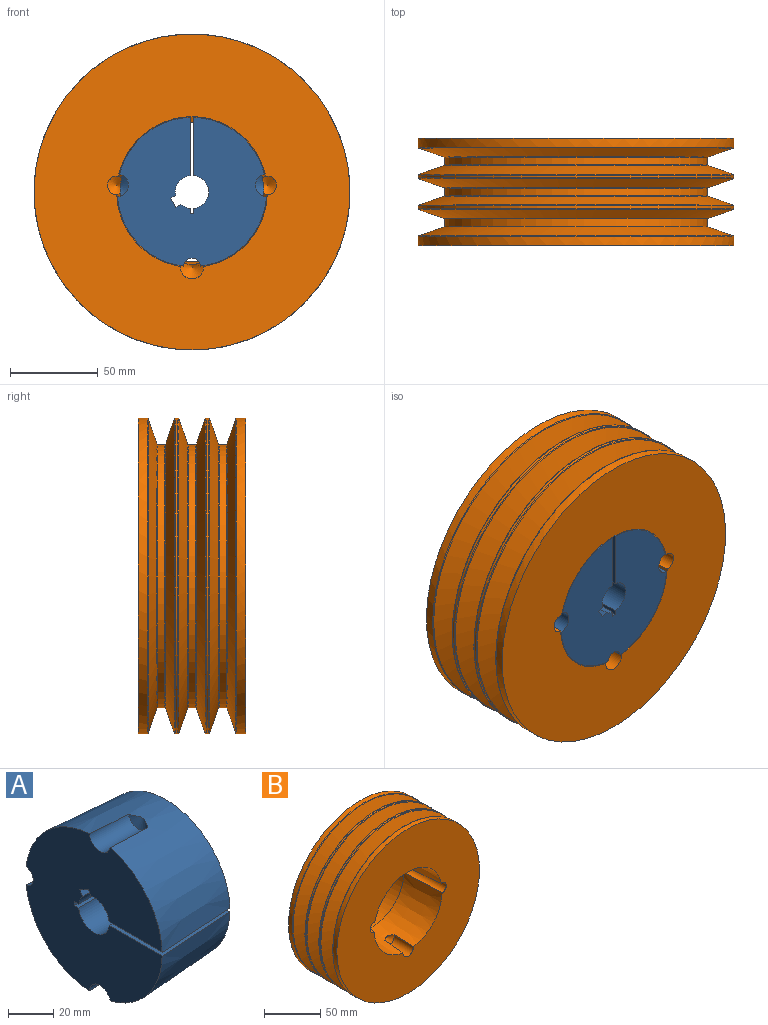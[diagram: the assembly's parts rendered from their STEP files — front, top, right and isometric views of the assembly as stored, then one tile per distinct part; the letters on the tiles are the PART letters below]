
ASSEMBLY  parts=2 mates=1
PART A: 20 faces, bbox 45x84.8x85 mm
  f0: cone r=39.69mm half-angle=3.6deg, axis (-1,0,0), area 5249.3mm2, adj f4,f6,f7,f15,f18,f19
  f1: cone r=39.69mm half-angle=3.6deg, axis (-1,0,0), area 5249.3mm2, adj f4,f6,f8,f15,f16,f17
  f2: cylinder r=9.5mm len=45mm, axis (1,0,0), area 712.9mm2, adj f4,f6,f8,f13
  f3: cylinder r=9.5mm len=45mm, axis (1,0,0), area 265.2mm2, adj f4,f6,f9,f14
  f4: plane 84.82x84.7mm, normal (-1,0,0), area 5146.6mm2, adj f0,f1,f2,f3,f5,f7,f8,f9
  f5: cylinder r=9.5mm len=45mm, axis (1,0,0), area 1252.9mm2, adj f4,f6,f7,f10
  f6: plane 79.38x79.19mm, normal (1,0,0), area 4571.4mm2, adj f0,f1,f2,f3,f5,f7,f8,f9
  f7: plane 45x33.04mm, normal (0,0,1), area 1423.5mm2, adj f0,f4,f5,f6
  f8: plane 45x33.04mm, normal (0,0,-1), area 1423.5mm2, adj f1,f2,f4,f6
  f9: plane 45x2.85mm, normal (0,0,-1), area 128.4mm2, adj f3,f4,f6,f11
  f10: plane 45x2.85mm, normal (0,0,1), area 128.4mm2, adj f4,f5,f6,f11
  f11: plane 45x2mm, normal (0,-1,0), area 90mm2, adj f4,f6,f9,f10
  f12: plane 45x5.2mm, normal (0,-0.5,-0.87), area 270mm2, adj f4,f6,f13,f14
  f13: plane 45x2.85mm, normal (0,0.87,-0.5), area 147.9mm2, adj f2,f4,f6,f12
  f14: plane 45x2.85mm, normal (0,-0.87,0.5), area 147.9mm2, adj f3,f4,f6,f12
  f15: cylinder r=5mm len=45mm, axis (1,0,0), area 515.4mm2, adj f0,f1,f4,f6
  f16: cone r=0mm half-angle=60deg, axis (-1,0,0), area 46mm2, adj f1,f17
  f17: cylinder r=6.5mm len=24mm, axis (-1,0,0), area 414.5mm2, adj f1,f4,f16
  f18: cone r=0mm half-angle=60deg, axis (-1,0,0), area 46mm2, adj f0,f19
  f19: cylinder r=6.5mm len=24mm, axis (-1,0,0), area 414.5mm2, adj f0,f4,f18
PART B: 40 faces, bbox 194.8x61x194.8 mm
  f0: plane 180x180mm, normal (0,-1,0), area 19496.2mm2, adj f1,f34,f35,f36,f38,f39
  f1: cylinder r=5.36mm len=45mm, axis (0,-1,0), area 936.2mm2, adj f0,f2,f34,f36
  f2: cone r=0mm half-angle=59deg, axis (0,-1,0), area 90.3mm2, adj f1,f3,f4,f33
  f3: cone r=42.92mm half-angle=4deg, axis (0,-1,0), area 0mm2, adj f2,f4
  f4: cylinder r=39.78mm len=79.56mm, axis (0,-1,0), area 3985.1mm2, adj f2,f3,f5,f6,f7,f8,f33,f34
  f5: cone r=42.92mm half-angle=4deg, axis (0,-1,0), area 0mm2, adj f4,f6
  f6: cone r=0mm half-angle=59deg, axis (0,-1,0), area 90.3mm2, adj f4,f5,f7,f35
  f7: cone r=42.92mm half-angle=4deg, axis (0,-1,0), area 0mm2, adj f4,f6
  f8: plane 180x180mm, normal (0,1,0), area 20475.5mm2, adj f4,f9
  f9: cylinder r=90mm len=180mm, axis (0,-1,0), area 2840.6mm2, adj f8,f10
  f10: torus R=89.5mm, axis (0,1,0), area 349.9mm2, adj f9,f11
  f11: cone r=75mm half-angle=71deg, axis (0,1,0), area 7853.7mm2, adj f10,f12
  f12: torus R=75.5mm, axis (0,-1,0), area 292.4mm2, adj f11,f13
  f13: cylinder r=75mm len=150mm, axis (0,-1,0), area 1977.7mm2, adj f12,f14
  f14: torus R=75.5mm, axis (0,-1,0), area 292.4mm2, adj f13,f15
  f15: cone r=90mm half-angle=71deg, axis (0,-1,0), area 7853.7mm2, adj f14,f16
  f16: torus R=89.5mm, axis (0,1,0), area 349.9mm2, adj f15,f17
  f17: cylinder r=90mm len=180mm, axis (0,-1,0), area 874.6mm2, adj f16,f18
  f18: torus R=89.5mm, axis (0,1,0), area 349.9mm2, adj f17,f19
  f19: cone r=75mm half-angle=71deg, axis (0,1,0), area 7853.7mm2, adj f18,f20
  f20: torus R=75.5mm, axis (0,-1,0), area 292.4mm2, adj f19,f21
  f21: cylinder r=75mm len=150mm, axis (0,-1,0), area 1977.7mm2, adj f20,f22
  f22: torus R=75.5mm, axis (0,-1,0), area 292.4mm2, adj f21,f23
  f23: cone r=90mm half-angle=71deg, axis (0,-1,0), area 7853.7mm2, adj f22,f24
  f24: torus R=89.5mm, axis (0,1,0), area 349.9mm2, adj f23,f25
  f25: cylinder r=90mm len=180mm, axis (0,-1,0), area 874.6mm2, adj f24,f26
  f26: torus R=89.5mm, axis (0,1,0), area 349.9mm2, adj f25,f27
  f27: cone r=75mm half-angle=71deg, axis (0,1,0), area 7853.7mm2, adj f26,f28
  f28: torus R=75.5mm, axis (0,-1,0), area 292.4mm2, adj f27,f29
  f29: cylinder r=75mm len=150mm, axis (0,-1,0), area 1977.7mm2, adj f28,f30
  f30: torus R=75.5mm, axis (0,-1,0), area 292.4mm2, adj f29,f31
  f31: cone r=90mm half-angle=71deg, axis (0,-1,0), area 7853.7mm2, adj f30,f32
  f32: torus R=89.5mm, axis (0,1,0), area 349.9mm2, adj f31,f39
  f33: cone r=42.92mm half-angle=4deg, axis (0,-1,0), area 0mm2, adj f2,f4
  f34: cone r=42.92mm half-angle=4deg, axis (0,-1,0), area 5088.6mm2, adj f0,f1,f4,f35
  f35: cylinder r=5.36mm len=45mm, axis (0,-1,0), area 936.2mm2, adj f0,f6,f34,f36
  f36: cone r=42.92mm half-angle=4deg, axis (0,-1,0), area 5410.3mm2, adj f0,f1,f4,f35,f37,f38
  f37: cone r=0mm half-angle=59deg, axis (0,-1,0), area 108mm2, adj f36,f38
  f38: cylinder r=6.55mm len=24mm, axis (0,-1,0), area 558.3mm2, adj f0,f36,f37
  f39: cylinder r=90mm len=180mm, axis (0,-1,0), area 2840.6mm2, adj f0,f32
PLACE A rot(axis=(-0.58,-0.58,0.58),120deg) t=(0,-30.5,0)mm
PLACE B at identity
MATE cylindrical A.f0 <-> B.f3  axis (0,-1,0) through (0,-30.5,0)mm
